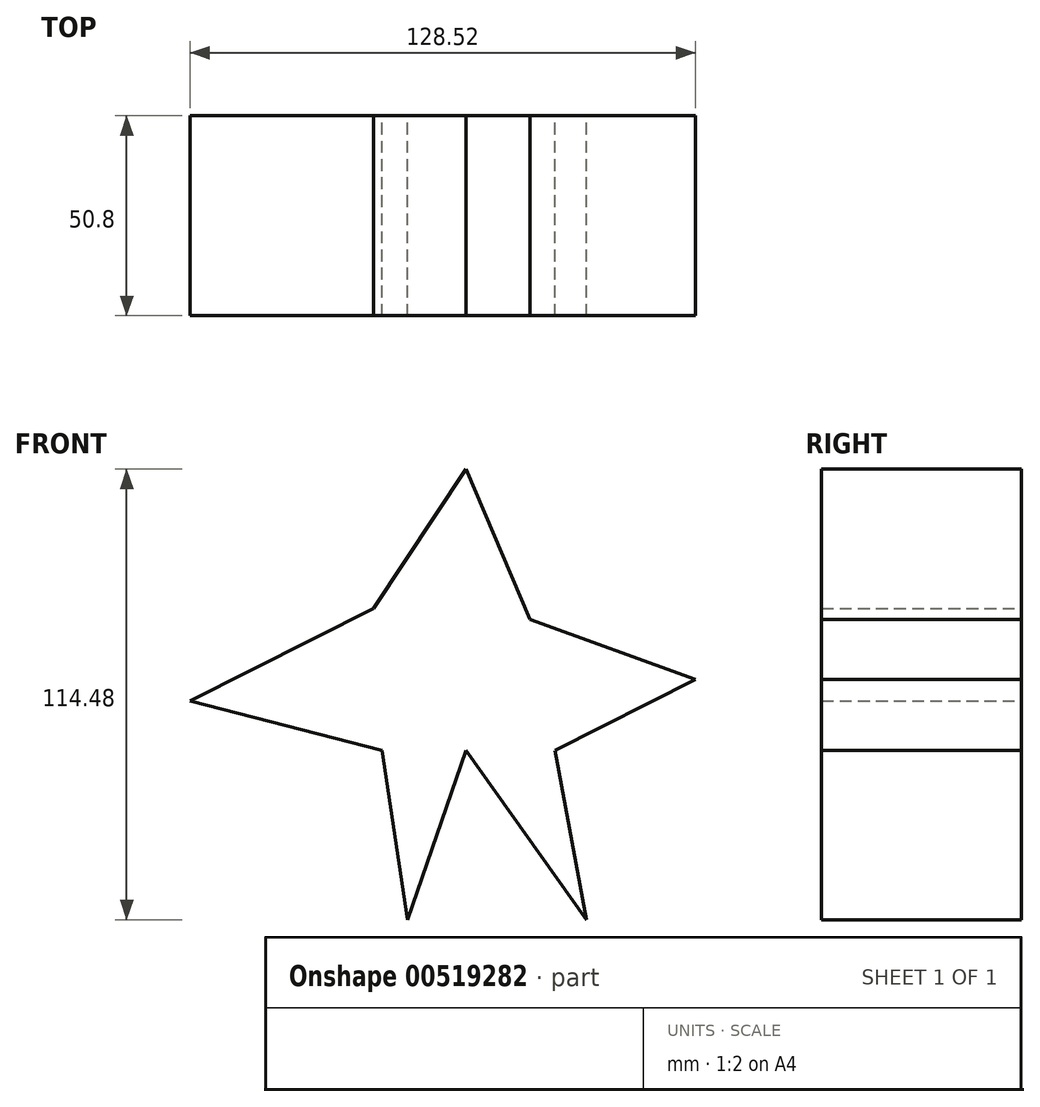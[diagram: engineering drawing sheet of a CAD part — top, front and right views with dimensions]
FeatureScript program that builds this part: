
annotation { "Feature Type Name" : "Feature", "Feature Type Description" : "" }
export const myFeature = defineFeature(function(context is Context, id is Id, definition is map)
    precondition{}
    {
        {
            var Q0;
            Q0=qCreatedBy(makeId("Front.planeOp"),FACE);
            var sketch = newSketch(context, id + "F0", { "sketchPlane" : qUnion([Q0])});
            skLineSegment(sketch, "E0", {"start": v(-23.5, 23.5) * mm, "end": v(-70.21, 0) * mm});
            skLineSegment(sketch, "E1", {"start": v(-70.21, 0) * mm, "end": v(-21.37, -12.52) * mm});
            skLineSegment(sketch, "E2", {"start": v(-21.37, -12.52) * mm, "end": v(-14.96, -55.56) * mm});
            skLineSegment(sketch, "E3", {"start": v(-14.96, -55.56) * mm, "end": v(0, -12.52) * mm});
            skLineSegment(sketch, "E4", {"start": v(0, -12.52) * mm, "end": v(30.53, -55.56) * mm});
            skLineSegment(sketch, "E5", {"start": v(30.53, -55.56) * mm, "end": v(22.59, -12.52) * mm});
            skLineSegment(sketch, "E6", {"start": v(22.59, -12.52) * mm, "end": v(58.3, 5.5) * mm});
            skLineSegment(sketch, "E7", {"start": v(58.3, 5.5) * mm, "end": v(16.18, 20.76) * mm});
            skLineSegment(sketch, "E8", {"start": v(16.18, 20.76) * mm, "end": v(0, 58.92) * mm});
            skLineSegment(sketch, "E9", {"start": v(0, 58.92) * mm, "end": v(-23.5, 23.5) * mm});
            skSolve(sketch);
        }
        {
            var Q0;
            Q0=makeQuery(id+"F0.imprint","IMPRINT",FACE,{"disambiguationData":[TD([[makeQuery(id+"F0.imprint","IMPRINT",EDGE,{"derivedFrom":sQuery(id+"F0.wireOp",EDGE,"E0")}),1.0]])]});
            extrude(context, id + "F1", {"entities" : qUnion([Q0]), "depth" : 50.8 * mm, "offsetDistance" : 25.4 * mm});
        }
    });
